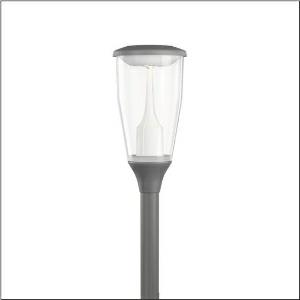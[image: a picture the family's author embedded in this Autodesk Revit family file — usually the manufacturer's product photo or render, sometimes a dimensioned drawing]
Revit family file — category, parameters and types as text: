
# Revit family: dl_11_iq___st1_2a_5xa5575af14hp00022_5e00
name_source: partatom
category: Lighting Fixtures
units: mm (PartAtom-declared; Revit-internal decimal feet)

## family parameters
Cut with Voids When Loaded = No
Host = Face
Light Source = No
Part Type = Normal
Room Calculation Point = No
Round Connector Dimension = Use Diameter
Shared = No

## types (1)
- --- (1 x LED, 4000 lm, 33.6 W, 2200K)
    Apparent Load = 34 VA
    CIE Flux Codes = 23 60 93 95 100
    Color Rendering = 70
    Color Temperature = 2200K
    Default Elevation = 1800 mm
    Description = DL 11 iQ, mast luminaire, Module 540 iQ-SR, primary light control with 3 zone facetted reflector, of plastic, silver coated, highly specular, structured, primary optical cover: cover, of PMMA, transparent, light distribution: ST1.2a, light emission: direct distribution, primary light characteristic: asymmetric, installation type: post-top, LED, High Power LED, rated luminous flux: 4.000lm, luminous efficacy: 119lm/W, light colour: 722, colour temperature: 2200K, control gear: iQ Street-Remote, control: Street-Remote, Auto-Match, Temp-Guard, Lumen-Switch, Night-Set, Smart-Wire, Light-Fading, Desk-Remote (wireless, voltage-free reading and setting of iQ features in the workshop via application-optimized NFC function/RFID function), optimised constant luminous flux control (CLO 2.0), mains connection: 220..240V, AC, 50/60Hz, connection cable pre-assembled, cable length: 5,5m, start of lifetime: 34W, end of service life: 36W, reduction: 15W, luminaire housing, upper part, of diecast aluminium, coated, SITECO metallic grey (DB 702S), spigot size: 76mm (post-top), mounting height: 3..5m, post-top mast mounting element, of diecast aluminium, coated, SITECO metallic grey (DB 702S), Module 540 iQ-SR, traffic white (RAL 9016), equipment: Power, protection rating (complete): IP66, insulation class (complete): insulation class II (safety insulation), certification: CE, ENEC, ENEC+, VDE, impact resistance: IK07, packaging unit: 1 piece

Light Distribution: ST1.2a
    Height = 665 mm
    Lamp = 1 x LED
    Lamp Light Flux = 4000 lm
    Lamp Power = 33.6 W
    Lamp count = 1
    Length = 334 mm
    Luminous efficacy = 119 lm/W
    Manufacturer = Siteco
    ModVariant = No
    Model = 5XA5575AF14HP00022
    Number of Poles = 1
    OnlyDefault = Yes
    Power Factor = 1
    Product Name = DL 11 iQ | ST1.2a
    Product group = mast luminaire | pylon top
    ProductGroupID = 6100
    Protection Class = Protection class II
    Protection Degree = IP 66
    RLX_Detail_Level = 1
    RLX_Emergency_Light_Flux = 0 lm
    RLX_Emergency_Type = 0
    RLX_Emergency_Type_DB = No
    RlxData = <blob elided: 155849 chars, md5=e489fb83>
    Socket = socket
    Standby Power = 0 W
    System Light Flux = 4000 lm
    System Power = 34 W
    Type Comments = factory setting: luminous flux: 100 % | dim-lin: 254 | 695 mA
    Type Image = l_1258354.jpg
    URL = http://relux.com
    VarID = @adj_040197
    Voltage = 0 V
    Weight = 0.00 kg
    Width = 0 mm  [stored 0 ft]

note: [stored X ft] marks values corroborated as IEEE doubles in the binary element streams (Revit-internal decimal feet)

## geometry (parser evidence)
native form markers: Blend x4, Sweep x11
no freeform markers — native parametric forms only
